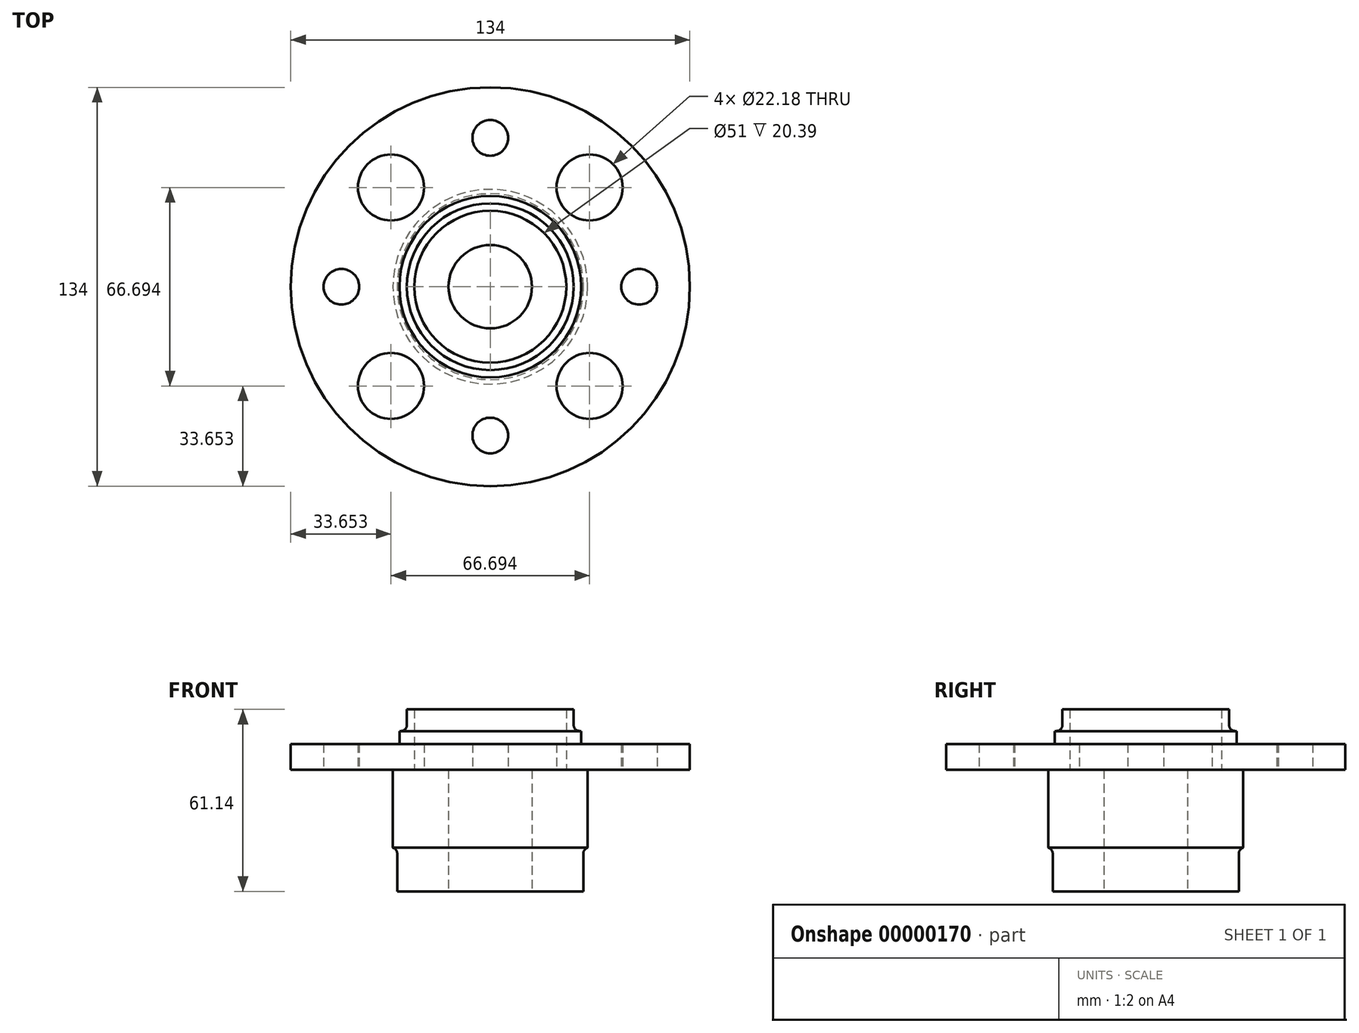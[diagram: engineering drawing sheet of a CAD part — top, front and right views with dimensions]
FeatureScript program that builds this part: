
annotation { "Feature Type Name" : "Feature", "Feature Type Description" : "" }
export const myFeature = defineFeature(function(context is Context, id is Id, definition is map)
    precondition{}
    {
        {
            var Q0;
            Q0=qCreatedBy(makeId("Top.planeOp"),FACE);
            var sketch = newSketch(context, id + "F0", { "sketchPlane" : qUnion([Q0])});
            skCircle(sketch, "E0", {"center": v(0, 0) * mm, "radius": 31.25 * mm});
            skSolve(sketch);
        }
        {
            var Q0;
            Q0=makeQuery(id+"F0.imprint","IMPRINT",FACE,{"disambiguationData":[TD([[makeQuery(id+"F0.imprint","IMPRINT",EDGE,{"derivedFrom":sQuery(id+"F0.wireOp",EDGE,"E0")}),1.0]])]});
            var Q1;
            Q1=sQuery(id+"F0.wireOp",EDGE,"E0");
            extrude(context, id + "F1", {"entities" : qUnion([Q0]), "surfaceEntities" : qUnion([Q1]), "depth" : 40 * mm});
        }
        {
            var Q0;
            Q0=qCreatedBy(makeId("Top.planeOp"),FACE);
            cPlane(context, id + "F2", {"entities" : qUnion([Q0]), "cplaneType" : CPlaneType.OFFSET, "offset" : 14.62 * mm, "width" : 150 * mm, "height" : 150 * mm});
        }
        {
            var Q0;
            Q0=qCreatedBy(id+"F2.planeOp",FACE);
            var sketch = newSketch(context, id + "F3", { "sketchPlane" : qUnion([Q0])});
            skCircle(sketch, "E1", {"center": v(0, 0) * mm, "radius": 32.7 * mm});
            skSolve(sketch);
        }
        {
            var Q0;
            Q0=makeQuery(id+"F3.imprint","IMPRINT",FACE,{"disambiguationData":[TD([[makeQuery(id+"F3.imprint","IMPRINT",EDGE,{"derivedFrom":sQuery(id+"F3.wireOp",EDGE,"E1")}),1.0]])]});
            var Q1;
            Q1=sQuery(id+"F3.wireOp",EDGE,"E1");
            extrude(context, id + "F4", {"entities" : qUnion([Q0]), "operationType" : NewBodyOperationType.ADD, "surfaceEntities" : qUnion([Q1]), "depth" : 26.22 * mm});
        }
        {
            var Q0;
            Q0=qCreatedBy(makeId("Top.planeOp"),FACE);
            cPlane(context, id + "F5", {"entities" : qUnion([Q0]), "cplaneType" : CPlaneType.OFFSET, "offset" : 40.84 * mm, "width" : 150 * mm, "height" : 150 * mm});
        }
        {
            var Q0;
            Q0=qCreatedBy(id+"F5.planeOp",FACE);
            var sketch = newSketch(context, id + "F6", { "sketchPlane" : qUnion([Q0])});
            skCircle(sketch, "E2", {"center": v(0, 0) * mm, "radius": 67 * mm});
            skCircle(sketch, "E3", {"center": v(-33.35, 33.35) * mm, "radius": 11.1 * mm});
            skCircle(sketch, "E4", {"center": v(33.35, 33.35) * mm, "radius": 11.1 * mm});
            skCircle(sketch, "E5", {"center": v(-33.35, -33.35) * mm, "radius": 11.1 * mm});
            skCircle(sketch, "E6", {"center": v(33.35, -33.35) * mm, "radius": 11.1 * mm});
            skLineSegment(sketch, "E7.bottom", {"start": v(-33.35, 33.35) * mm, "end": v(33.35, 33.35) * mm, "construction": true});
            skLineSegment(sketch, "E7.top", {"start": v(-33.35, -33.35) * mm, "end": v(33.35, -33.35) * mm, "construction": true});
            skLineSegment(sketch, "E7.left", {"start": v(-33.35, 33.35) * mm, "end": v(-33.35, -33.35) * mm, "construction": true});
            skLineSegment(sketch, "E7.right", {"start": v(33.35, 33.35) * mm, "end": v(33.35, -33.35) * mm, "construction": true});
            skCircle(sketch, "E8", {"center": v(0, 50) * mm, "radius": 6 * mm});
            skCircle(sketch, "E9", {"center": v(0, 0) * mm, "radius": 50 * mm, "construction": true});
            skLineSegment(sketch, "E10", {"start": v(0, 0) * mm, "end": v(0, 50) * mm, "construction": true});
            skCircle(sketch, "E11", {"center": v(-50, 0) * mm, "radius": 6 * mm});
            skCircle(sketch, "E12", {"center": v(0, -50) * mm, "radius": 6 * mm});
            skCircle(sketch, "E13", {"center": v(50, 0) * mm, "radius": 6 * mm});
            skSolve(sketch);
        }
        {
            var Q0;
            Q0=makeQuery(id+"F6.imprint","IMPRINT",FACE,{"disambiguationData":[TD([[makeQuery(id+"F6.imprint","IMPRINT",EDGE,{"derivedFrom":sQuery(id+"F6.wireOp",EDGE,"E2")}),1.0]])]});
            extrude(context, id + "F7", {"entities" : qUnion([Q0]), "operationType" : NewBodyOperationType.ADD, "depth" : 8.7 * mm});
        }
        {
            var Q0;
            Q0=qCreatedBy(makeId("Top.planeOp"),FACE);
            var sketch = newSketch(context, id + "F8", { "sketchPlane" : qUnion([Q0])});
            skCircle(sketch, "E14", {"center": v(0, 0) * mm, "radius": 14 * mm});
            skSolve(sketch);
        }
        {
            var Q0;
            Q0=qCreatedBy(id+"F5.planeOp",FACE);
            cPlane(context, id + "F9", {"entities" : qUnion([Q0]), "cplaneType" : CPlaneType.OFFSET, "offset" : 8.7 * mm, "width" : 150 * mm, "height" : 150 * mm});
        }
        {
            var Q0;
            Q0=qCreatedBy(id+"F9.planeOp",FACE);
            var sketch = newSketch(context, id + "F10", { "sketchPlane" : qUnion([Q0])});
            skCircle(sketch, "E15", {"center": v(0, 0) * mm, "radius": 30.5 * mm});
            skSolve(sketch);
        }
        {
            var Q0;
            Q0=makeQuery(id+"F10.imprint","IMPRINT",FACE,{"disambiguationData":[TD([[makeQuery(id+"F10.imprint","IMPRINT",EDGE,{"derivedFrom":sQuery(id+"F10.wireOp",EDGE,"E15")}),1.0]])]});
            var Q1;
            Q1=sQuery(id+"F10.wireOp",EDGE,"E15");
            extrude(context, id + "F11", {"entities" : qUnion([Q0]), "operationType" : NewBodyOperationType.ADD, "surfaceEntities" : qUnion([Q1]), "depth" : 4.32 * mm});
        }
        {
            var Q0;
            Q0=qCreatedBy(id+"F9.planeOp",FACE);
            var sketch = newSketch(context, id + "F12", { "sketchPlane" : qUnion([Q0])});
            skCircle(sketch, "E16", {"center": v(0, 0) * mm, "radius": 28 * mm});
            skSolve(sketch);
        }
        {
            var Q0;
            Q0=makeQuery(id+"F12.imprint","IMPRINT",FACE,{"disambiguationData":[TD([[makeQuery(id+"F12.imprint","IMPRINT",EDGE,{"derivedFrom":sQuery(id+"F12.wireOp",EDGE,"E16")}),1.0]])]});
            extrude(context, id + "F13", {"entities" : qUnion([Q0]), "operationType" : NewBodyOperationType.ADD, "depth" : 11.6 * mm});
        }
        {
            var Q0;
            Q0=makeQuery(id+"F8.imprint","IMPRINT",FACE,{"disambiguationData":[TD([[makeQuery(id+"F8.imprint","IMPRINT",EDGE,{"derivedFrom":sQuery(id+"F8.wireOp",EDGE,"E14")}),1.0]])]});
            extrude(context, id + "F14", {"entities" : qUnion([Q0]), "operationType" : NewBodyOperationType.REMOVE, "endBound" : BoundingType.THROUGH_ALL, "depth" : 25 * mm});
        }
        {
            var Q0;
            Q0=qCreatedBy(makeId("Top.planeOp"),FACE);
            cPlane(context, id + "F15", {"entities" : qUnion([Q0]), "cplaneType" : CPlaneType.OFFSET, "offset" : 40.75 * mm, "width" : 150 * mm, "height" : 150 * mm});
        }
        {
            var Q0;
            Q0=qCreatedBy(id+"F15.planeOp",FACE);
            var sketch = newSketch(context, id + "F16", { "sketchPlane" : qUnion([Q0])});
            skCircle(sketch, "E17", {"center": v(0, 0) * mm, "radius": 25.5 * mm});
            skSolve(sketch);
        }
        {
            var Q0;
            Q0=makeQuery(id+"F16.imprint","IMPRINT",FACE,{"disambiguationData":[TD([[makeQuery(id+"F16.imprint","IMPRINT",EDGE,{"derivedFrom":sQuery(id+"F16.wireOp",EDGE,"E17")}),1.0]])]});
            extrude(context, id + "F17", {"entities" : qUnion([Q0]), "operationType" : NewBodyOperationType.REMOVE, "endBound" : BoundingType.THROUGH_ALL, "depth" : 25 * mm});
        }
        {
            var Q0;
            Q0=makeQuery(id+"F13.boolean.opBoolean","INTERSECT",EDGE,{"derivedFrom":[makeQuery(id+"F11.opExtrude","CAP_FACE",FACE,{"disambiguationData":[OSD([sQuery(id+"F10.wireOp",EDGE,"E15")])],"isStart":false}),makeQuery(id+"F13.opExtrude","SWEPT_FACE",FACE,{"disambiguationData":[OSD([sQuery(id+"F12.wireOp",EDGE,"E16")])]})]});
            var Q1;
            Q1=makeQuery(id+"F11.opExtrude","CAP_EDGE",EDGE,{"disambiguationData":[OSD([sQuery(id+"F10.wireOp",EDGE,"E15")])],"isStart":true});
            var Q2;
            Q2=makeQuery(id+"F4.opExtrude","CAP_EDGE",EDGE,{"disambiguationData":[OSD([sQuery(id+"F3.wireOp",EDGE,"E1")])],"isStart":false});
            var Q3;
            Q3=makeQuery(id+"F4.boolean.opBoolean","INTERSECT",EDGE,{"derivedFrom":[makeQuery(id+"F1.opExtrude","SWEPT_FACE",FACE,{"disambiguationData":[OSD([sQuery(id+"F0.wireOp",EDGE,"E0")])]}),makeQuery(id+"F4.opExtrude","CAP_FACE",FACE,{"disambiguationData":[OSD([sQuery(id+"F3.wireOp",EDGE,"E1")])],"isStart":true})]});
            fillet(context, id + "F18", {"entities" : qUnion([Q0, Q1, Q2, Q3]), "radius" : 2 * mm, "tangentPropagation" : true, "allowEdgeOverflow" : false});
        }
    });
